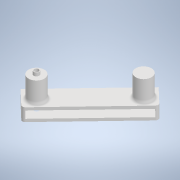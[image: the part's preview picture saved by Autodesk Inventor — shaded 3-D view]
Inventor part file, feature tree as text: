
AUTODESK INVENTOR PART (.ipt)
format: ipt  version: 2022 (Build 260153000, 153)  size: 338,432 bytes
history: native  units: in
note: dims shown in document units (in); Inventor stores cm internally (conversion verified against a paired STEP export)
features: extrude x16, sketch x14, projected_geometry x10, plane x5, other x5, reference x4, fillet x3, mirror x1
ambient origin geometry x8: Origin, YZ Plane, XZ Plane, XY Plane, X Axis, Y Axis, Z Axis, Center Point
bodies: Solid1 (feature_tree)
feature tree (58):
  extrude  "Extrusion1"  Depth=1.9685in
  extrude  "Extrusion2"  Depth=0.5512in
  extrude  "Extrusion3"  Depth=0.7066in
  sketch  "Sketch5"  dims[d7=1.0846in d8=0.9843in]
  extrude  "Extrusion5"  Depth=0.9843in
  extrude  "Extrusion6"  Depth=0.7087in TaperAngle=0.0deg
  plane  "Work Plane1"
  extrude  "Extrusion7"  Depth=0.1929in
  extrude  "Extrusion8"  Depth=0.1516in
  extrude  "Extrusion9"  Depth=1.9685in TaperAngle=0.0deg
  fillet  "Fillet1"  Radius=0.0079in
  fillet  "Fillet2"  Radius=0.0079in
  sketch  "Sketch11"  dims[d29=0.7874in d30=0.0984in]
  extrude  "Extrusion10"  Depth=0.0984in
  sketch  "Sketch12"  dims[d31=0.0984in d32=0.7874in]
  plane  "Work Plane2"
  extrude  "Extrusion11"  Depth=0.7874in
  extrude  "Extrusion12"  Depth=0.0984in
  fillet  "Fillet3"  [1 undecoded]
  plane  "Work Plane3"
  mirror  "Mirror1"
  sketch  "Sketch14"  dims[d37=0.0984in d38=0.252in d39=0.0in]
  plane  "Work Plane4"
  extrude  "Extrusion13"  Depth=0.252in TaperAngle=0.0deg
  sketch  "Sketch15"  dims[d40=0.0984in d41=0.0in d42=0.0984in]
  plane  "Work Plane5"
  extrude  "Extrusion14"  Depth=0.0984in
  extrude  "Extrusion15"  Depth=0.3228in
  extrude  "Extrusion16"  Depth=0.3937in TaperAngle=0.0deg
  extrude  "Extrusion17"  Depth=0.3937in TaperAngle=0.0deg
  sketch  "Sketch1"  dims[d0=3.937in d1=1.9685in]
  sketch  "Sketch2"  dims[d2=0.1181in d3=0.0in d4=0.5512in]
  sketch  "Sketch3"  dims[d5=0.5512in d6=0.7066in]
  projected_geometry  "Projected Loop1"
  projected_geometry  "Projected Loop2"
  sketch  "Sketch7"  dims[d9=0.9843in d10=0.7087in d11=0.0in]
  projected_geometry  "Projected Loop4"
  sketch  "Sketch8"  dims[d12=0.2264in d13=0.1929in]
  reference  "Reference1"
  reference  "Reference2"
  reference  "Reference3"
  reference  "Reference4"
  sketch  "Sketch9"  dims[d14=0.1181in d15=0.0in d20=0.1516in]
  projected_geometry  "Projected Loop5"
  sketch  "Sketch10"  dims[d21=0.5906in d22=0.0in d24=1.9685in d25=0.0in d26=0.0079in d27=0.0079in]
  projected_geometry  "Projected Loop6"
  projected_geometry  "Projected Loop7"
  projected_geometry  "Projected Loop8"
  sketch  "Sketch13"  dims[d33=0.0984in d34=0.0in d35=0.0984in d36=0.0in]
  projected_geometry  "Projected Loop9"
  projected_geometry  "Projected Loop10"
  sketch  "Sketch16"  dims[d43=0.0984in d44=0.3228in d45=0.0591in d46=0.0in d47=2.5268in d48=0.0in d49=0.0984in d50=0.0in d51=0.0984in d52=-1.7063in d53=0.0984in d54=0.0in d55=0.3937in d56=0.0in d57=0.0591in d58=0.0in d59=0.0591in d60=0.0in d61=0.7874in d62=0.0in d63=0.0197in d64=0.0344in]
  projected_geometry  "Projected Loop11"
  other  "<userpath>\OneDrive\Desktop\P3\2. Hopper Assembly\Updated_Hopper_Mechanism.iam"
  other  "Updated_Hopper_Mechanism.iam"
  other  "Connecting_Plate:1"
  other  "HopperVR41Y_Base:1"
  other  "92095A199_Button Head Hex Drive Screw:1"
note: 1 required parameter value undecoded (feature->parameter linkage not recoverable at this tier; creation-order binding heuristic only, values carry confidence <= 0.55)
